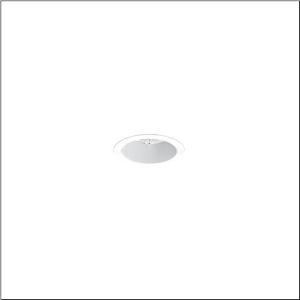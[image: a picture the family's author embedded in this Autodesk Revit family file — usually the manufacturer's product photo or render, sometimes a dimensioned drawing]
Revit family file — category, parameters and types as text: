
# Revit family: lunis_21_s_51db18ma91c
name_source: partatom
category: Lighting Fixtures
units: mm (PartAtom-declared; Revit-internal decimal feet)

## family parameters
Cut with Voids When Loaded = No
Host = Face
Light Source = No
Part Type = Normal
Room Calculation Point = No
Round Connector Dimension = Use Diameter
Shared = No

## types (1)
- --- (1 x LED, 980 lm, 5.9 W, 4000K)
    Apparent Load = 6 VA
    CIE Flux Codes = 95 100 100 100 100
    Color Rendering = 80
    Color Temperature = 4000K
    Default Elevation = 1800 mm
    Description = Lunis 21,  S, downlight, light control with lens, of PMMA, anti glare with reflector, of PC, light emission: direct distribution, LED rated luminous flux: 980lm, light colour: 830/840/865, with terminal, 3-pole, mains connection: 220..240V, AC, 50..60Hz, housing, round, of diecast aluminium, traffic white (RAL 9016), diameter: 84mm, clamping range: 1..40mm, protection rating (complete): IP20, protection rating (on room side): IP54, insulation class (complete): insulation class II (safety insulation), certification: CE, impact resistance: IK03, packaging unit: 1 piece
    Height = 0 mm  [stored 0 ft]
    Lamp = 1 x LED
    Lamp Light Flux = 980 lm
    Lamp Power = 5.9 W
    Lamp count = 1
    Length = 84 mm
    Luminous efficacy = 166 lm/W
    Manufacturer = Siteco
    ModVariant = No
    Model = 51DB18MA91C
    Mounting Place = Ceiling
    Mounting Type = Recessed
    Number of Poles = 1
    OnlyDefault = Yes
    Power Factor = 1
    Product Name = Lunis 21 S
    Product group = downlight
    ProductGroupID = 401
    Protection Class = Protection class II
    Protection Degree = IP 20
    RLX_Detail_Level = 1
    RLX_Emergency_Light_Flux = 0 lm
    RLX_Emergency_Type = 0
    RLX_Emergency_Type_DB = No
    RlxData = <blob elided: 7397 chars, md5=a7fbb64b>
    Socket = socket
    Standby Power = 0 W
    System Light Flux = 980 lm
    System Power = 6 W
    Type Comments = factory setting: colour temperature 4000K
    Type Image = l_1290842.jpg
    URL = http://relux.com
    VarID = @adj_025993
    Voltage = 0 V
    Weight = 0.00 kg
    Width = 0 mm  [stored 0 ft]

note: [stored X ft] marks values corroborated as IEEE doubles in the binary element streams (Revit-internal decimal feet)

## geometry (parser evidence)
native form markers: Sweep x9
no freeform markers — native parametric forms only
